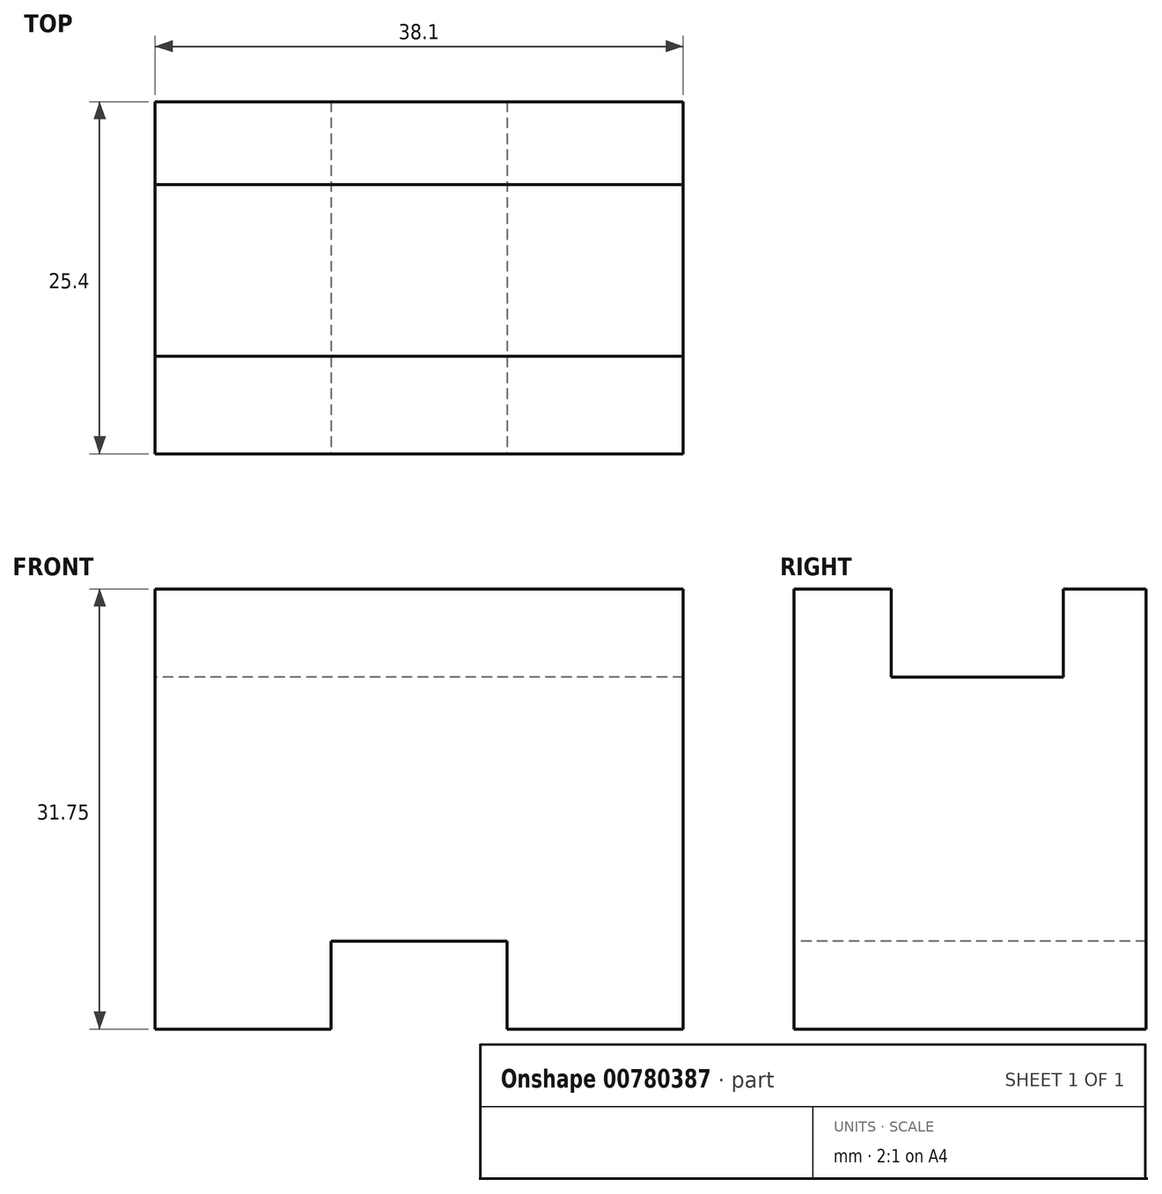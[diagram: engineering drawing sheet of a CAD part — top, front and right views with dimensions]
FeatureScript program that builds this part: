
annotation { "Feature Type Name" : "Feature", "Feature Type Description" : "" }
export const myFeature = defineFeature(function(context is Context, id is Id, definition is map)
    precondition{}
    {
        {
            var Q0;
            Q0=qCreatedBy(makeId("Front.planeOp"),FACE);
            var sketch = newSketch(context, id + "F0", { "sketchPlane" : qUnion([Q0])});
            skLineSegment(sketch, "E0", {"start": v(0, 0) * mm, "end": v(38.1, 0) * mm});
            skLineSegment(sketch, "E1", {"start": v(38.1, 0) * mm, "end": v(38.1, 31.75) * mm});
            skLineSegment(sketch, "E2", {"start": v(38.1, 31.75) * mm, "end": v(0, 31.75) * mm});
            skLineSegment(sketch, "E3", {"start": v(0, 31.75) * mm, "end": v(0, 0) * mm});
            skSolve(sketch);
        }
        {
            var Q0;
            Q0=makeQuery(id+"F0.imprint","IMPRINT",FACE,{"disambiguationData":[TD([[makeQuery(id+"F0.imprint","IMPRINT",EDGE,{"derivedFrom":sQuery(id+"F0.wireOp",EDGE,"E0")}),1.0]])]});
            extrude(context, id + "F1", {"entities" : qUnion([Q0]), "depth" : 25.4 * mm, "offsetDistance" : 25.4 * mm});
        }
        {
            var Q0;
            Q0=makeQuery(id+"F1.opExtrude","SWEPT_FACE",FACE,{"disambiguationData":[OSD([sQuery(id+"F0.wireOp",EDGE,"E2")])]});
            var sketch = newSketch(context, id + "F2", { "sketchPlane" : qUnion([Q0])});
            skLineSegment(sketch, "E4", {"start": v(38.1, -5.99) * mm, "end": v(0, -5.99) * mm});
            skLineSegment(sketch, "E5", {"start": v(38.1, -18.37) * mm, "end": v(0, -18.37) * mm});
            skSolve(sketch);
        }
        {
            var Q0;
            {var subQ0=sQuery(id+"F2.wireOp",EDGE,"E4");Q0=makeQuery(id+"F2.imprint","IMPRINT",FACE,{"disambiguationData":[TD([[makeQuery(id+"F2.imprint","IMPRINT",EDGE,{"derivedFrom":subQ0}),1.0]])]});}
            extrude(context, id + "F3", {"entities" : qUnion([Q0]), "operationType" : NewBodyOperationType.REMOVE, "oppositeDirection" : true, "depth" : 6.35 * mm, "offsetDistance" : 25.4 * mm});
        }
        {
            var Q0;
            Q0=makeQuery(id+"F1.opExtrude","CAP_FACE",FACE,{"disambiguationData":[OSD([sQuery(id+"F0.wireOp",EDGE,"E0"),sQuery(id+"F0.wireOp",EDGE,"E1"),sQuery(id+"F0.wireOp",EDGE,"E2"),sQuery(id+"F0.wireOp",EDGE,"E3")])],"isStart":false});
            var sketch = newSketch(context, id + "F4", { "sketchPlane" : qUnion([Q0])});
            skLineSegment(sketch, "E6", {"start": v(0, 0) * mm, "end": v(12.7, 0) * mm});
            skLineSegment(sketch, "E7", {"start": v(38.1, 0) * mm, "end": v(25.4, 0) * mm});
            skLineSegment(sketch, "E8", {"start": v(12.7, 0) * mm, "end": v(12.7, 6.35) * mm});
            skLineSegment(sketch, "E9", {"start": v(25.4, 0) * mm, "end": v(25.4, 6.35) * mm});
            skLineSegment(sketch, "E10", {"start": v(12.7, 6.35) * mm, "end": v(25.4, 6.35) * mm});
            skSolve(sketch);
        }
        {
            var Q0;
            {var subQ0=sQuery(id+"F4.wireOp",EDGE,"E8");Q0=makeQuery(id+"F4.imprint","IMPRINT",FACE,{"disambiguationData":[TD([[makeQuery(id+"F4.imprint","IMPRINT",EDGE,{"derivedFrom":subQ0}),-1.0]])]});}
            extrude(context, id + "F5", {"entities" : qUnion([Q0]), "operationType" : NewBodyOperationType.REMOVE, "oppositeDirection" : true, "depth" : 25.4 * mm, "offsetDistance" : 25.4 * mm});
        }
    });
